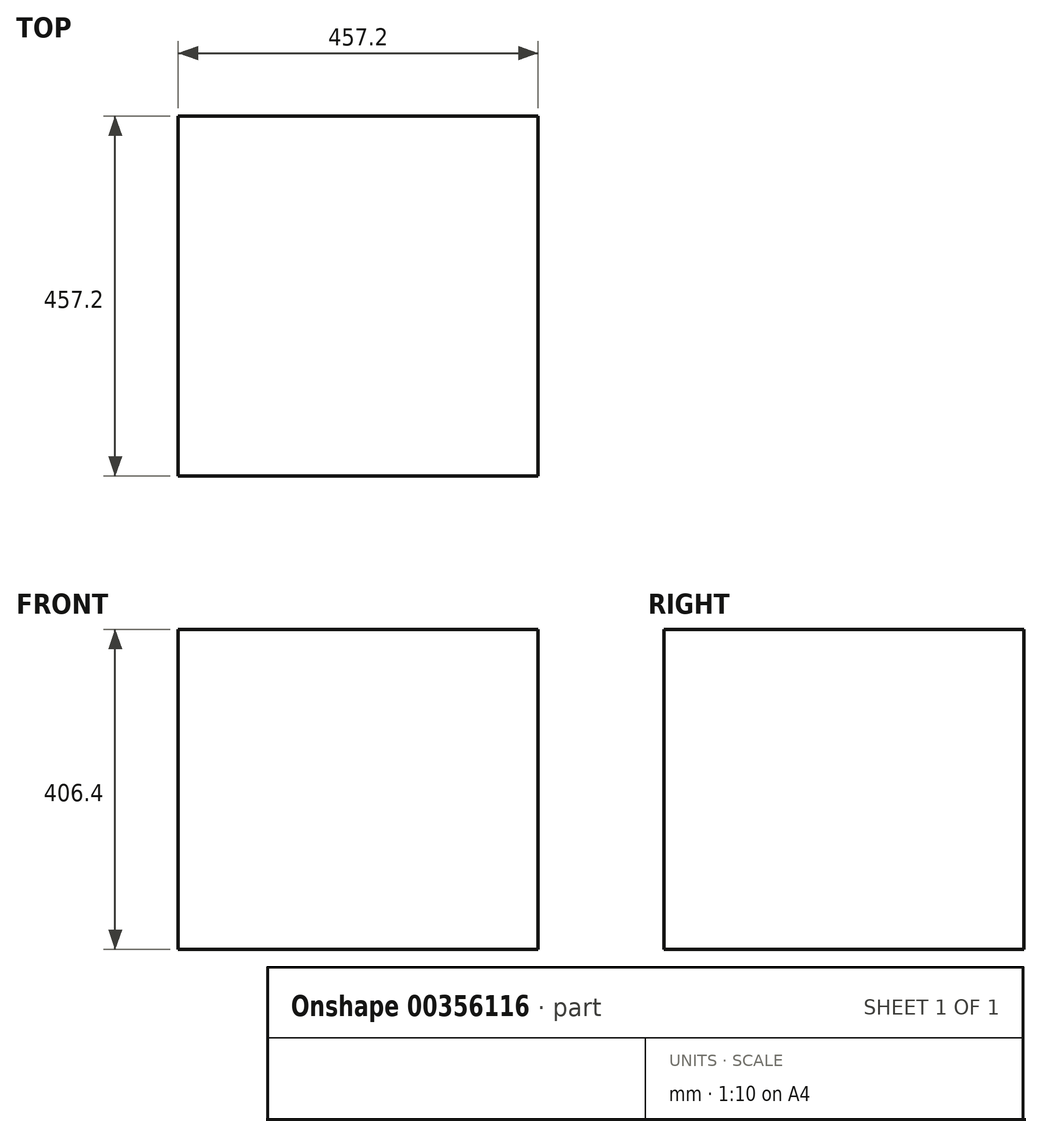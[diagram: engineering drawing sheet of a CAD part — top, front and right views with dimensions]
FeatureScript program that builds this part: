
annotation { "Feature Type Name" : "Feature", "Feature Type Description" : "" }
export const myFeature = defineFeature(function(context is Context, id is Id, definition is map)
    precondition{}
    {
        {
            var Q0;
            Q0=qCreatedBy(makeId("Top.planeOp"),FACE);
            var sketch = newSketch(context, id + "F0", { "sketchPlane" : qUnion([Q0])});
            skLineSegment(sketch, "E0.bottom", {"start": v(-228.6, -228.6) * mm, "end": v(228.6, -228.6) * mm});
            skLineSegment(sketch, "E0.top", {"start": v(-228.6, 228.6) * mm, "end": v(228.6, 228.6) * mm});
            skLineSegment(sketch, "E0.left", {"start": v(-228.6, -228.6) * mm, "end": v(-228.6, 228.6) * mm});
            skLineSegment(sketch, "E0.right", {"start": v(228.6, -228.6) * mm, "end": v(228.6, 228.6) * mm});
            skPoint(sketch, "E0.middle", {"position": v(0, 0) * mm});
            skSolve(sketch);
        }
        {
            var Q0;
            Q0=makeQuery(id+"F0.imprint","IMPRINT",FACE,{"disambiguationData":[TD([[makeQuery(id+"F0.imprint","IMPRINT",EDGE,{"derivedFrom":sQuery(id+"F0.wireOp",EDGE,"E0.bottom")}),1.0]])]});
            var Q1;
            Q1=sQuery(id+"F0.wireOp",EDGE,"E0.top");
            extrude(context, id + "F1", {"entities" : qUnion([Q0]), "surfaceEntities" : qUnion([Q1]), "depth" : 406.4 * mm, "offsetDistance" : 25.4 * mm});
        }
    });
